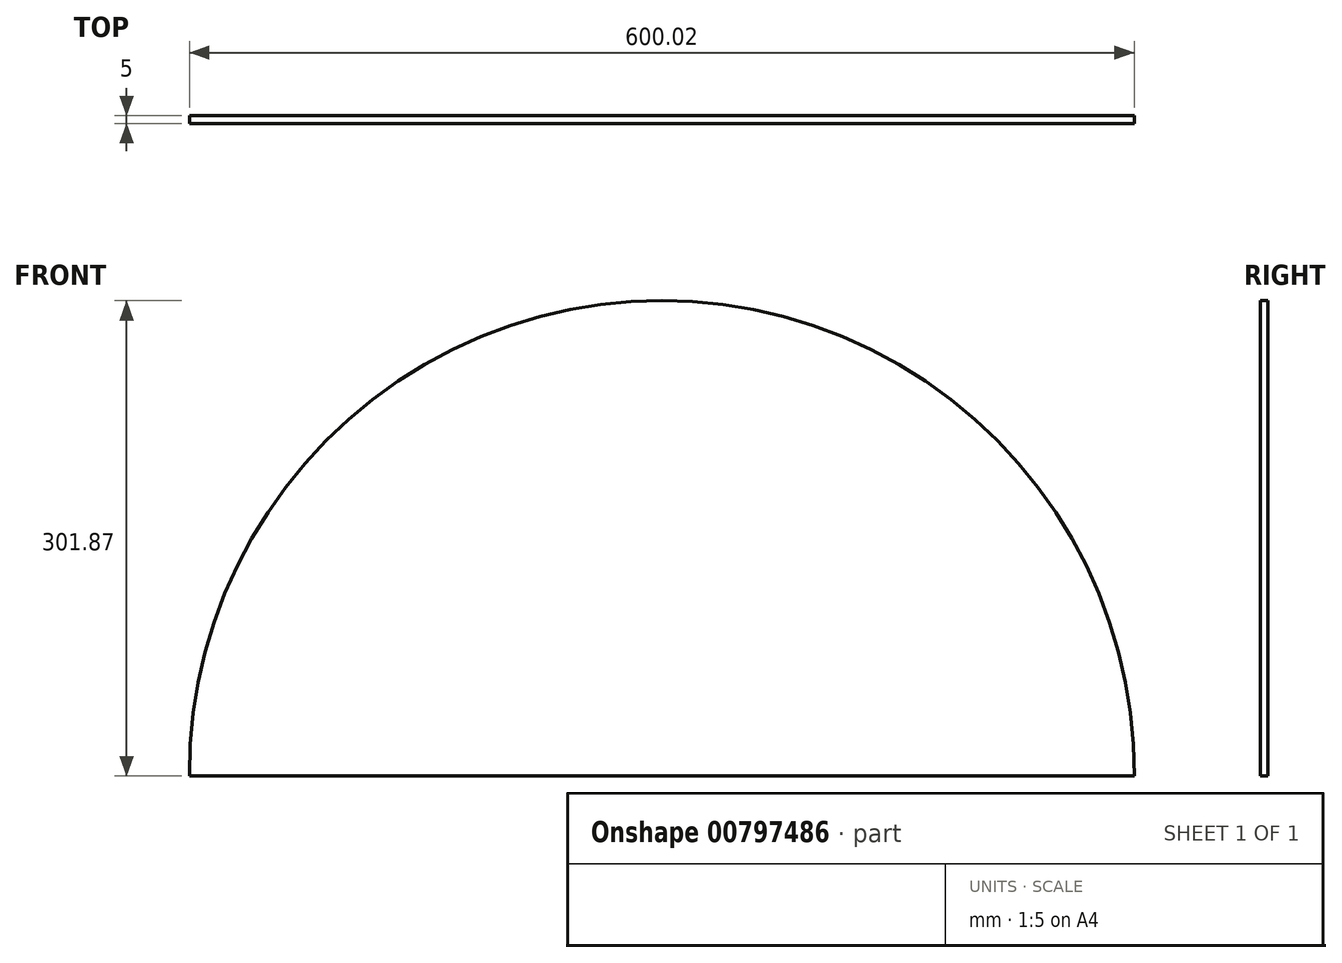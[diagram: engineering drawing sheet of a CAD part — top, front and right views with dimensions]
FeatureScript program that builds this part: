
annotation { "Feature Type Name" : "Feature", "Feature Type Description" : "" }
export const myFeature = defineFeature(function(context is Context, id is Id, definition is map)
    precondition{}
    {
        {
            var Q0;
            Q0=qCreatedBy(makeId("Front.planeOp"),FACE);
            var sketch = newSketch(context, id + "F0", { "sketchPlane" : qUnion([Q0])});
            skLineSegment(sketch, "E0", {"start": v(-600, 0) * mm, "end": v(0, 0) * mm});
            skArc(sketch, "E1", {"start": v(0, 0) * mm, "mid": v(-300, 301.87) * mm, "end": v(-600, 0) * mm});
            skSolve(sketch);
        }
        {
            var Q0;
            Q0=makeQuery(id+"F0.imprint","IMPRINT",FACE,{"disambiguationData":[TD([[makeQuery(id+"F0.imprint","IMPRINT",EDGE,{"derivedFrom":sQuery(id+"F0.wireOp",EDGE,"E0")}),1.0]])]});
            extrude(context, id + "F1", {"entities" : qUnion([Q0]), "depth" : 5 * mm, "offsetDistance" : 25 * mm});
        }
    });
